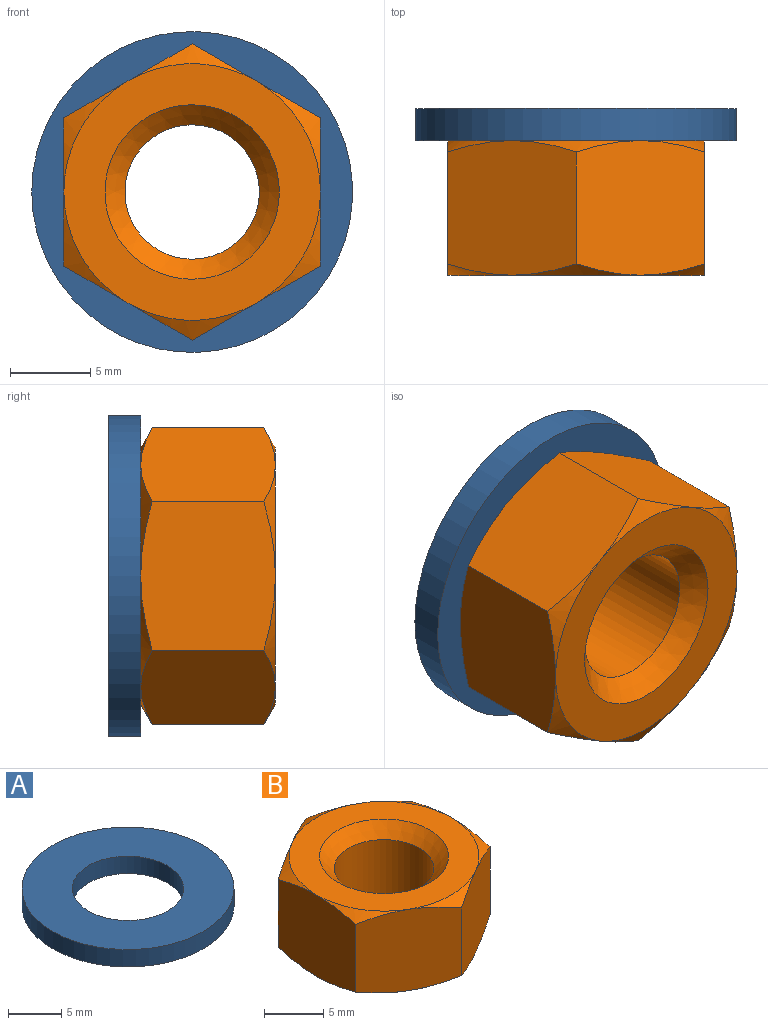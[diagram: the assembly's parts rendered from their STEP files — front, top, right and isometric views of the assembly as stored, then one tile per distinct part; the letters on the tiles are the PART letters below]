
ASSEMBLY  parts=2 mates=1
PART A: 4 faces, bbox 20x20x2 mm
  f0: cylinder r=5.25mm len=10.5mm, axis (0,0,-1), area 66mm2, adj f1,f3
  f1: plane 20x20mm, normal (0,0,-1), area 227.6mm2, adj f0,f2
  f2: cylinder r=10mm len=20mm, axis (0,0,-1), area 125.7mm2, adj f1,f3
  f3: plane 20x20mm, normal (0,0,1), area 227.6mm2, adj f0,f2
PART B: 23 faces, bbox 19.2x19.2x9.2 mm
  f0: plane 16x16mm, normal (0,0,1), area 108.2mm2, adj f15,f16,f17,f18,f19,f20,f21
  f1: plane 16x16mm, normal (0,0,-1), area 108.2mm2, adj f9,f10,f11,f12,f13,f14,f22
  f2: plane 10.01x9.17mm, normal (1,0,0), area 73.1mm2, adj f3,f7,f9,f14,f15,f20
  f3: plane 9.17x8.76mm, normal (0.5,0.87,0), area 73.1mm2, adj f2,f4,f13,f14,f19,f20
  f4: plane 9.17x8.76mm, normal (-0.5,0.87,0), area 73.1mm2, adj f3,f5,f12,f13,f18,f19
  f5: plane 10.01x9.17mm, normal (-1,0,0), area 73.1mm2, adj f4,f6,f11,f12,f17,f18
  f6: plane 9.17x8.76mm, normal (-0.5,-0.87,0), area 73.1mm2, adj f5,f7,f10,f11,f16,f17
  f7: plane 9.17x8.76mm, normal (0.5,-0.87,0), area 73.1mm2, adj f2,f6,f9,f10,f15,f16
  f8: cylinder r=4.19mm len=8.38mm, axis (0,0,-1), area 155.3mm2, adj f21,f22
  f9: cone r=15.27mm half-angle=60deg, axis (0,0,1), area 6.3mm2, adj f1,f2,f7
  f10: cone r=15.27mm half-angle=60deg, axis (0,0,1), area 6.3mm2, adj f1,f6,f7
  f11: cone r=15.27mm half-angle=60deg, axis (0,0,1), area 6.3mm2, adj f1,f5,f6
  f12: cone r=15.27mm half-angle=60deg, axis (0,0,1), area 6.3mm2, adj f1,f4,f5
  f13: cone r=15.27mm half-angle=60deg, axis (0,0,1), area 6.3mm2, adj f1,f3,f4
  f14: cone r=15.27mm half-angle=60deg, axis (0,0,1), area 6.3mm2, adj f1,f2,f3
  f15: cone r=15.27mm half-angle=60deg, axis (0,0,-1), area 6.3mm2, adj f0,f2,f7
  f16: cone r=15.27mm half-angle=60deg, axis (0,0,-1), area 6.3mm2, adj f0,f6,f7
  f17: cone r=15.27mm half-angle=60deg, axis (0,0,-1), area 6.3mm2, adj f0,f5,f6
  f18: cone r=15.27mm half-angle=60deg, axis (0,0,-1), area 6.3mm2, adj f0,f4,f5
  f19: cone r=15.27mm half-angle=60deg, axis (0,0,-1), area 6.3mm2, adj f0,f3,f4
  f20: cone r=15.27mm half-angle=60deg, axis (0,0,-1), area 6.3mm2, adj f0,f2,f3
  f21: cone r=4.19mm half-angle=45deg, axis (0,0,1), area 53.5mm2, adj f0,f8
  f22: cone r=5.44mm half-angle=45deg, axis (0,0,-1), area 53.5mm2, adj f1,f8
PLACE A rot(axis=(1,0,0),90deg) t=(-32,-8,10.5)mm
PLACE B rot(axis=(1,0,0),90deg) t=(-32,-10,10.5)mm
MATE fastened B.f8 <-> A.f0  axis (0,1,0) through (-32,-10,10.5)mm
